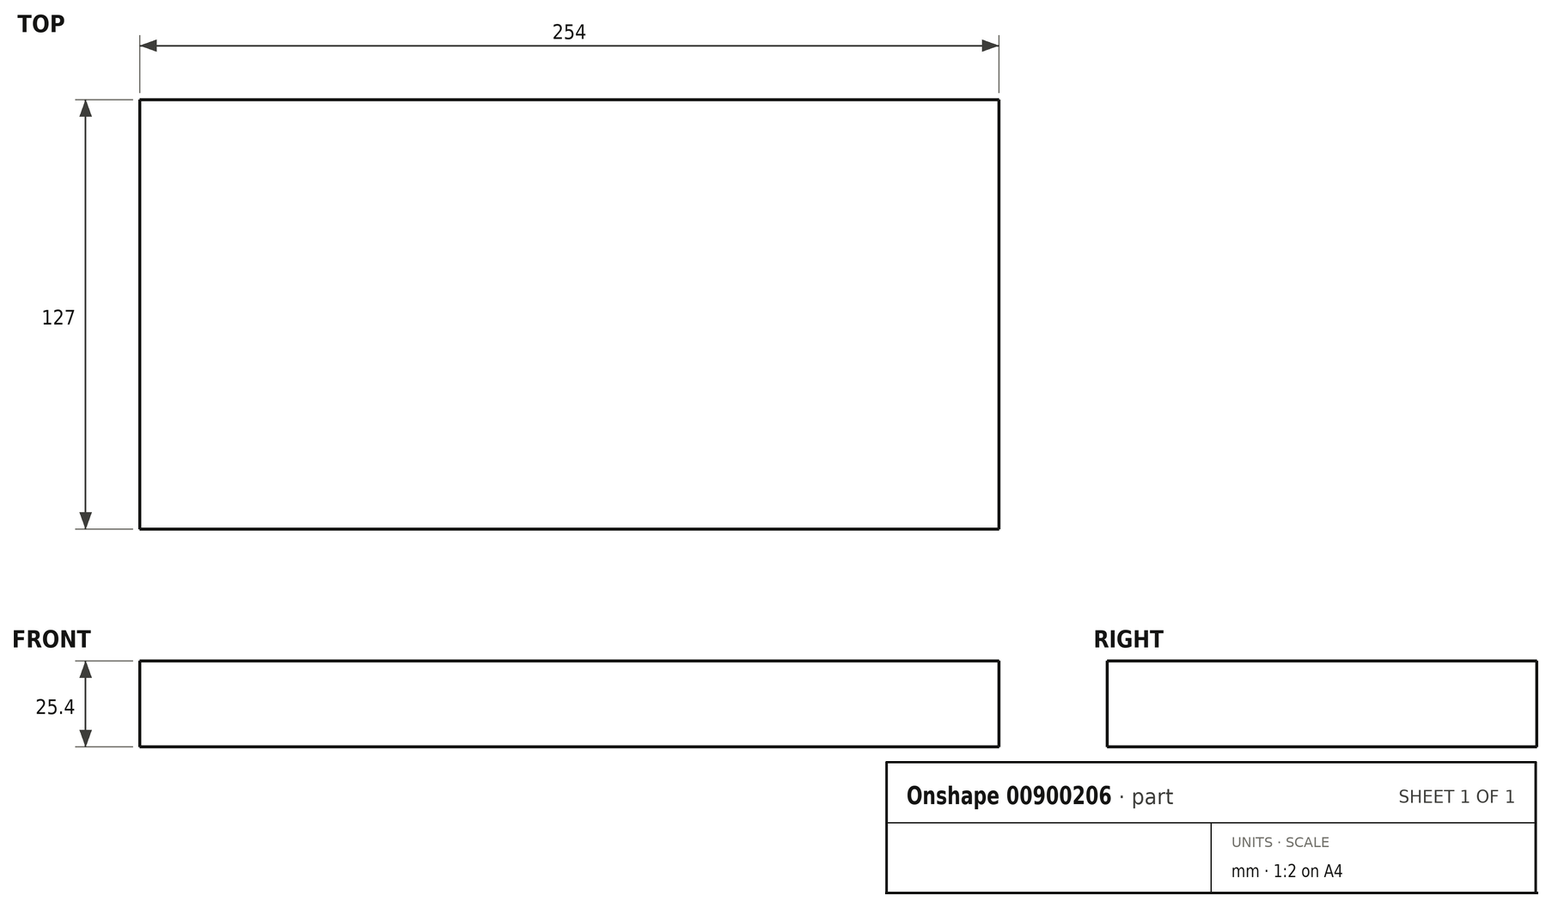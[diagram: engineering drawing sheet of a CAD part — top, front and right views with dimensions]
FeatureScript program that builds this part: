
annotation { "Feature Type Name" : "Feature", "Feature Type Description" : "" }
export const myFeature = defineFeature(function(context is Context, id is Id, definition is map)
    precondition{}
    {
        {
            var Q0;
            Q0=qCreatedBy(makeId("Top.planeOp"), FACE);
            var sketch = newSketch(context, id + "F0", { "sketchPlane" : qUnion([Q0])});
            skLineSegment(sketch, "E0.bottom", {"start": v(127, -63.5) * mm, "end": v(-127, -63.5) * mm});
            skLineSegment(sketch, "E0.top", {"start": v(127, 63.5) * mm, "end": v(-127, 63.5) * mm});
            skLineSegment(sketch, "E0.left", {"start": v(127, -63.5) * mm, "end": v(127, 63.5) * mm});
            skLineSegment(sketch, "E0.right", {"start": v(-127, -63.5) * mm, "end": v(-127, 63.5) * mm});
            skPoint(sketch, "E0.middle", {"position": v(0, 0) * mm, "construction": true});
            skSolve(sketch);
        }
        {
            var Q0;
            Q0 = qSketchRegion(id + "F0", true);
            extrude(context, id + "F1", {"entities" : qUnion([Q0]), "domain" : OperationDomain.MODEL, "flatOperationType" : FlatOperationType.REMOVE, "depth" : 25.4 * mm, "offsetDistance" : 25.4 * mm, "symmetric" : true});
        }
    });
